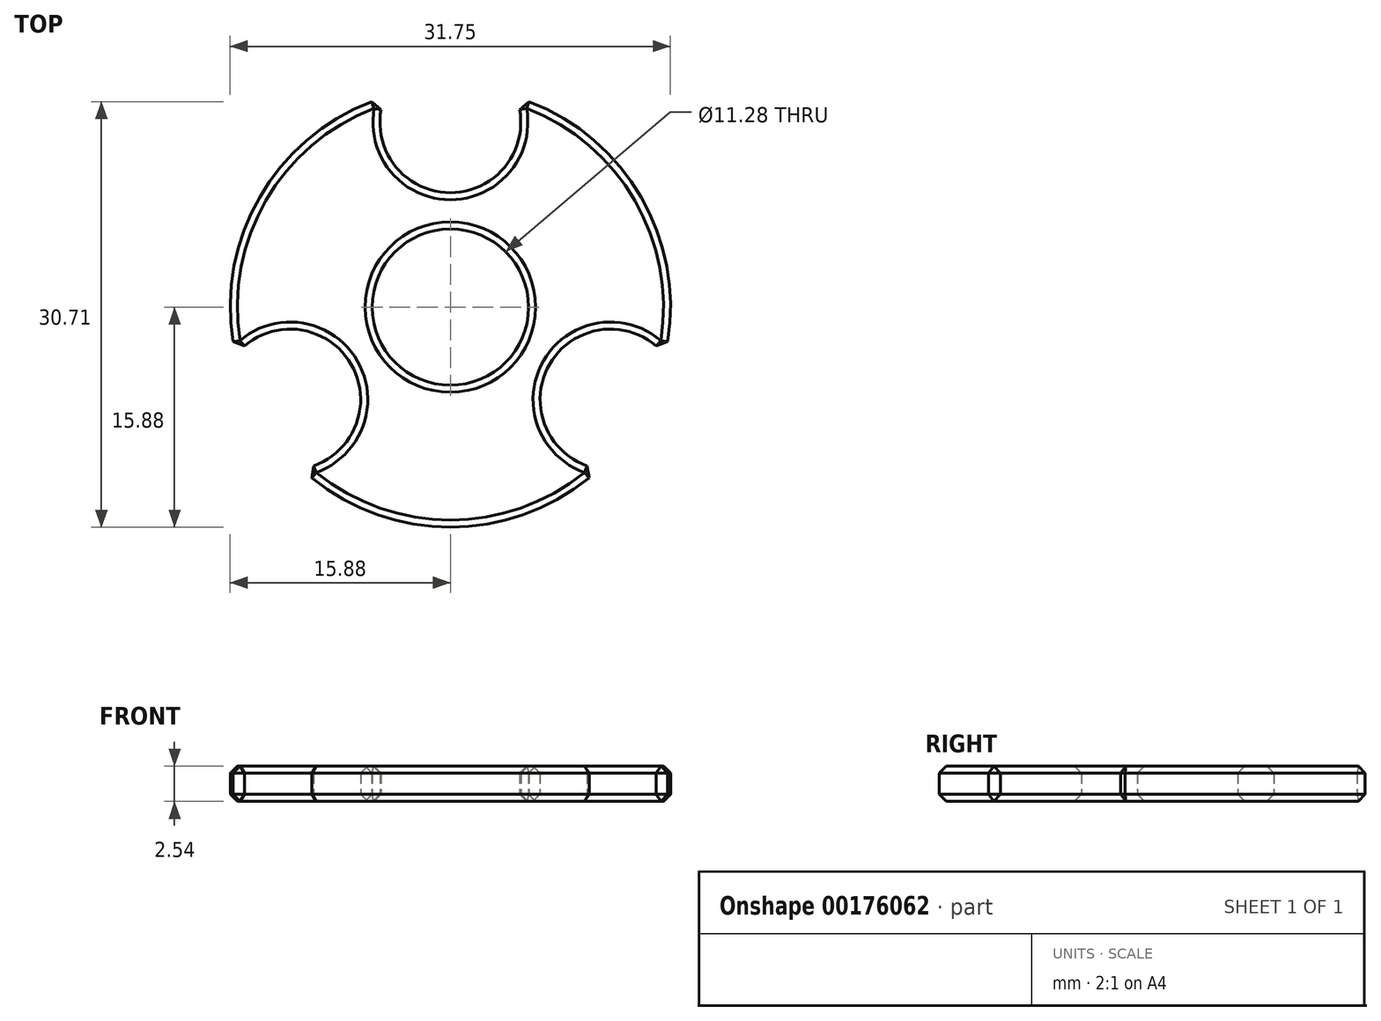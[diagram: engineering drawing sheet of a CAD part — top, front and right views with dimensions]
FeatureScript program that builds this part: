
annotation { "Feature Type Name" : "Feature", "Feature Type Description" : "" }
export const myFeature = defineFeature(function(context is Context, id is Id, definition is map)
    precondition{}
    {
        {
            var Q0;
            Q0=qCreatedBy(makeId("Top.planeOp"),FACE);
            var sketch = newSketch(context, id + "F0", { "sketchPlane" : qUnion([Q0])});
            skArc(sketch, "E0", {"start": v(-4.74, 15.15) * mm, "mid": v(-13.75, 7.94) * mm, "end": v(-15.5, -3.47) * mm});
            skArc(sketch, "E1", {"start": v(-4.74, 15.15) * mm, "mid": v(0, 8.25) * mm, "end": v(4.74, 15.15) * mm});
            skCircle(sketch, "E2", {"center": v(0, 0) * mm, "radius": 5.64 * mm});
            skArc(sketch, "E3.1.0", {"start": v(-10.75, -11.68) * mm, "mid": v(-7.15, -4.13) * mm, "end": v(-15.5, -3.47) * mm});
            skArc(sketch, "E3.2.0", {"start": v(15.5, -3.47) * mm, "mid": v(7.15, -4.13) * mm, "end": v(10.75, -11.68) * mm});
            skArc(sketch, "E4.trimOffspring", {"start": v(-10.75, -11.68) * mm, "mid": v(0, -15.88) * mm, "end": v(10.75, -11.68) * mm});
            skArc(sketch, "E5.trimOffspring", {"start": v(15.5, -3.47) * mm, "mid": v(13.75, 7.94) * mm, "end": v(4.74, 15.15) * mm});
            skSolve(sketch);
        }
        {
            var Q0;
            Q0=makeQuery(id+"F0.imprint","IMPRINT",FACE,{"disambiguationData":[TD([[makeQuery(id+"F0.imprint","IMPRINT",EDGE,{"derivedFrom":sQuery(id+"F0.wireOp",EDGE,"E0")}),1.0]])]});
            extrude(context, id + "F1", {"entities" : qUnion([Q0]), "depth" : 2.54 * mm});
        }
        {
            var Q0;
            Q0=makeQuery(id+"F1.opExtrude","CAP_FACE",FACE,{"disambiguationData":[OSD([sQuery(id+"F0.wireOp",EDGE,"E0"),sQuery(id+"F0.wireOp",EDGE,"E1"),sQuery(id+"F0.wireOp",EDGE,"E2"),sQuery(id+"F0.wireOp",EDGE,"E3.1.0"),sQuery(id+"F0.wireOp",EDGE,"E3.2.0"),sQuery(id+"F0.wireOp",EDGE,"E4.trimOffspring"),sQuery(id+"F0.wireOp",EDGE,"E5.trimOffspring")])],"isStart":false});
            var Q1;
            Q1=makeQuery(id+"F1.opExtrude","SWEPT_EDGE",EDGE,{"disambiguationData":[OSD([sQuery(id+"F0.wireOp",EDGE,"E3.2.0"),sQuery(id+"F0.wireOp",EDGE,"E4.trimOffspring")])]});
            var Q2;
            Q2=makeQuery(id+"F1.opExtrude","SWEPT_EDGE",EDGE,{"disambiguationData":[OSD([sQuery(id+"F0.wireOp",EDGE,"E3.2.0"),sQuery(id+"F0.wireOp",EDGE,"E5.trimOffspring")])]});
            var Q3;
            Q3=makeQuery(id+"F1.opExtrude","SWEPT_EDGE",EDGE,{"disambiguationData":[OSD([sQuery(id+"F0.wireOp",EDGE,"E0"),sQuery(id+"F0.wireOp",EDGE,"E3.1.0")])]});
            var Q4;
            Q4=makeQuery(id+"F1.opExtrude","SWEPT_EDGE",EDGE,{"disambiguationData":[OSD([sQuery(id+"F0.wireOp",EDGE,"E0"),sQuery(id+"F0.wireOp",EDGE,"E1")])]});
            var Q5;
            Q5=makeQuery(id+"F1.opExtrude","SWEPT_EDGE",EDGE,{"disambiguationData":[OSD([sQuery(id+"F0.wireOp",EDGE,"E3.1.0"),sQuery(id+"F0.wireOp",EDGE,"E4.trimOffspring")])]});
            var Q6;
            Q6=makeQuery(id+"F1.opExtrude","SWEPT_EDGE",EDGE,{"disambiguationData":[OSD([sQuery(id+"F0.wireOp",EDGE,"E1"),sQuery(id+"F0.wireOp",EDGE,"E5.trimOffspring")])]});
            var Q7;
            Q7=makeQuery(id+"F1.opExtrude","CAP_FACE",FACE,{"disambiguationData":[OSD([sQuery(id+"F0.wireOp",EDGE,"E0"),sQuery(id+"F0.wireOp",EDGE,"E1"),sQuery(id+"F0.wireOp",EDGE,"E2"),sQuery(id+"F0.wireOp",EDGE,"E3.1.0"),sQuery(id+"F0.wireOp",EDGE,"E3.2.0"),sQuery(id+"F0.wireOp",EDGE,"E4.trimOffspring"),sQuery(id+"F0.wireOp",EDGE,"E5.trimOffspring")])],"isStart":true});
            chamfer(context, id + "F2", {"entities" : qUnion([Q0, Q1, Q2, Q3, Q4, Q5, Q6, Q7]), "width" : 0.5 * mm, "tangentPropagation" : true});
        }
    });
